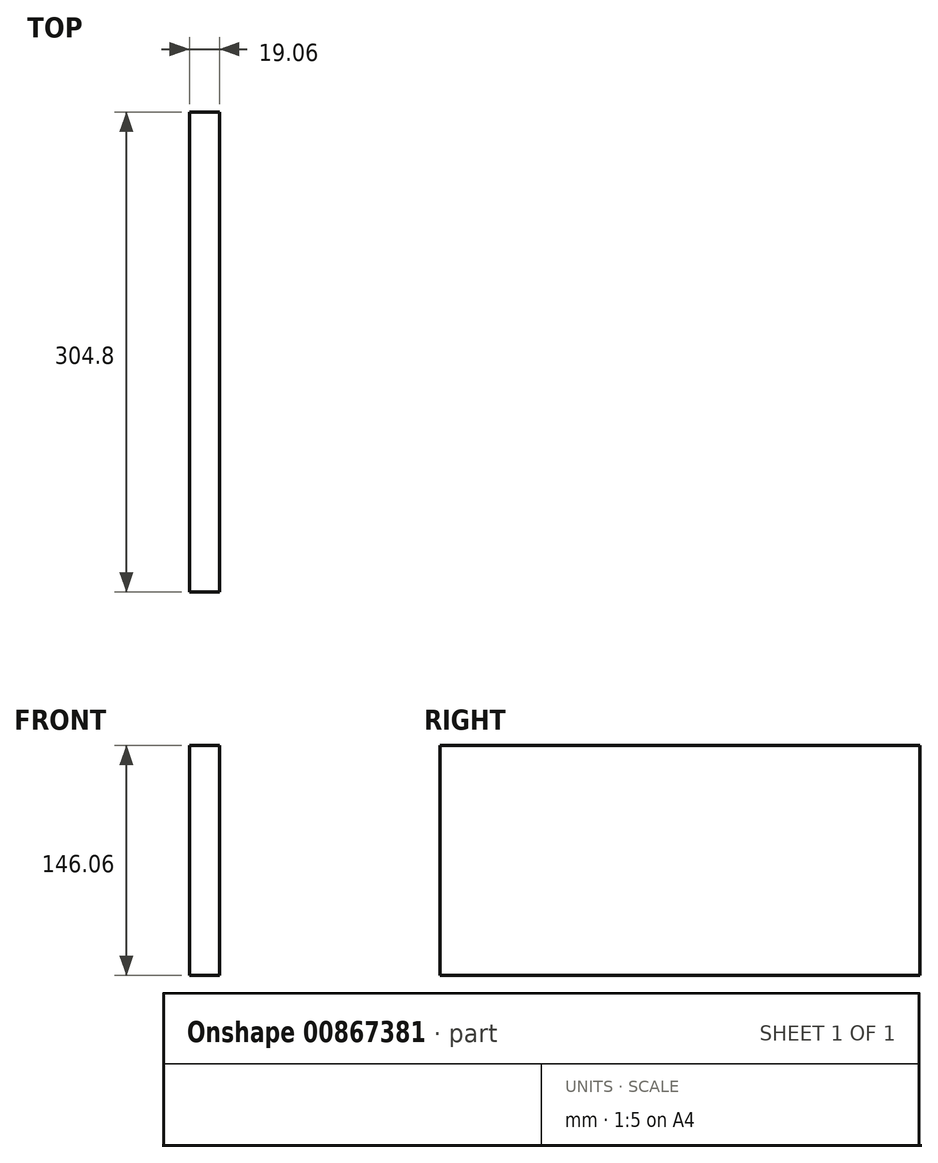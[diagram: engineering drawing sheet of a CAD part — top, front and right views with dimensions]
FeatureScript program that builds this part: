
annotation { "Feature Type Name" : "Feature", "Feature Type Description" : "" }
export const myFeature = defineFeature(function(context is Context, id is Id, definition is map)
    precondition{}
    {
        {
            var Q0;
            Q0=qCreatedBy(makeId("Front.planeOp"),FACE);
            var sketch = newSketch(context, id + "F0", { "sketchPlane" : qUnion([Q0])});
            skLineSegment(sketch, "E0.bottom", {"start": v(9.52, -73.03) * mm, "end": v(-9.53, -73.03) * mm});
            skLineSegment(sketch, "E0.top", {"start": v(9.52, 73.03) * mm, "end": v(-9.53, 73.03) * mm});
            skLineSegment(sketch, "E0.left", {"start": v(9.52, -73.03) * mm, "end": v(9.52, 73.03) * mm});
            skLineSegment(sketch, "E0.right", {"start": v(-9.53, -73.03) * mm, "end": v(-9.53, 73.03) * mm});
            skPoint(sketch, "E0.middle", {"position": v(0, 0) * mm});
            skSolve(sketch);
        }
        {
            var Q0;
            Q0 = qSketchRegion(id + "F0", true);
            extrude(context, id + "F1", {"entities" : qUnion([Q0]), "depth" : 304.8 * mm, "offsetDistance" : 25.4 * mm});
        }
    });
